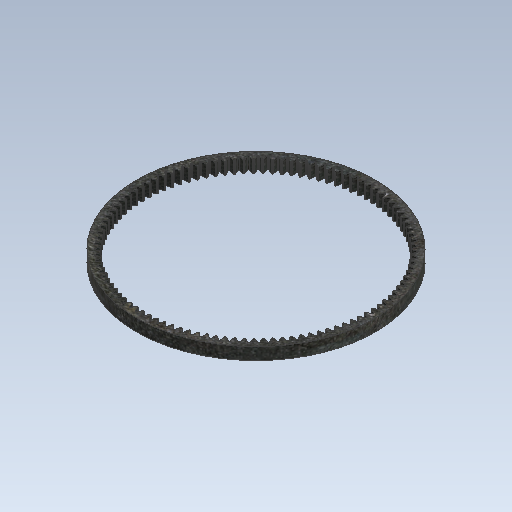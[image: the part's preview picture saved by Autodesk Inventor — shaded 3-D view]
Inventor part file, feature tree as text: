
AUTODESK INVENTOR PART (.ipt)
format: ipt  version: 2021 (Build 250183000, 183)  size: 1,062,400 bytes
history: native  units: mm
features: extrude x1, fillet x1, pattern_circular x1, sketch x1
ambient origin geometry x8: Origin, YZ Plane, XZ Plane, XY Plane, X Axis, Y Axis, Z Axis, Center Point
bodies: Solid1 (feature_tree)
feature tree (4):
  extrude  "Extrusion1"  Depth=0.4mm TaperAngle=360.0deg
  fillet  "Fillet2"  Radius=136.31068mm
  pattern_circular  "Circular Pattern2"  [2 undecoded]
  sketch  "Sketch1"  dims[d4=7.0mm d5=0.0mm d18=1030.0mm d19=360.0deg d23=136.31068mm d25=1.57767mm d26=1.262136mm d27=3.490659mm d28=122.160041mm d29=3.490659mm d30=0.315534mm d31=0.631068mm d32=0.991282mm d33=3.0mm d34=0.4mm d38=139.15534mm]
note: 2 required parameter values undecoded (feature->parameter linkage not recoverable at this tier; creation-order binding heuristic only, values carry confidence <= 0.55)
